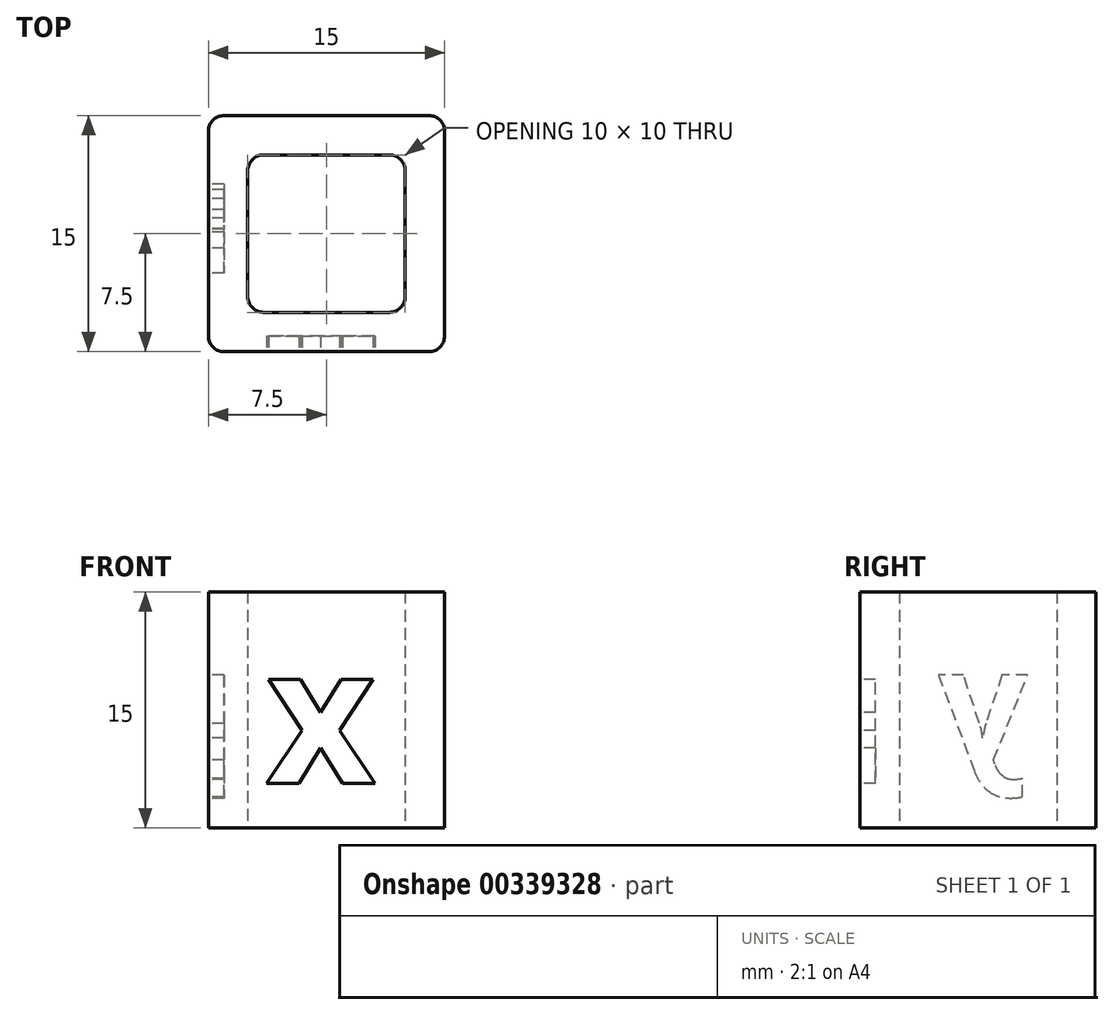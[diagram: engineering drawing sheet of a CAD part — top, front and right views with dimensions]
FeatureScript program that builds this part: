
annotation { "Feature Type Name" : "Feature", "Feature Type Description" : "" }
export const myFeature = defineFeature(function(context is Context, id is Id, definition is map)
    precondition{}
    {
        {
            var Q0;
            Q0=qCreatedBy(makeId("Top.planeOp"),FACE);
            var sketch = newSketch(context, id + "F0", { "sketchPlane" : qUnion([Q0])});
            skLineSegment(sketch, "E0.bottom", {"start": v(7.5, -7.5) * mm, "end": v(-7.5, -7.5) * mm});
            skLineSegment(sketch, "E0.top", {"start": v(7.5, 7.5) * mm, "end": v(-7.5, 7.5) * mm});
            skLineSegment(sketch, "E0.left", {"start": v(7.5, -7.5) * mm, "end": v(7.5, 7.5) * mm});
            skLineSegment(sketch, "E0.right", {"start": v(-7.5, -7.5) * mm, "end": v(-7.5, 7.5) * mm});
            skPoint(sketch, "E0.middle", {"position": v(0, 0) * mm});
            skLineSegment(sketch, "E1.bottom", {"start": v(5, -5) * mm, "end": v(-5, -5) * mm});
            skLineSegment(sketch, "E1.top", {"start": v(5, 5) * mm, "end": v(-5, 5) * mm});
            skLineSegment(sketch, "E1.left", {"start": v(5, -5) * mm, "end": v(5, 5) * mm});
            skLineSegment(sketch, "E1.right", {"start": v(-5, -5) * mm, "end": v(-5, 5) * mm});
            skSolve(sketch);
        }
        {
            var Q0;
            Q0=makeQuery(id+"F0.imprint","IMPRINT",FACE,{"disambiguationData":[TD([[makeQuery(id+"F0.imprint","IMPRINT",EDGE,{"derivedFrom":sQuery(id+"F0.wireOp",EDGE,"E0.bottom")}),-1.0]])]});
            extrude(context, id + "F1", {"entities" : qUnion([Q0]), "depth" : 15 * mm, "offsetDistance" : 25 * mm});
        }
        {
            var Q0;
            Q0=makeQuery(id+"F1.opExtrude","SWEPT_EDGE",EDGE,{"disambiguationData":[OSD([sQuery(id+"F0.wireOp",EDGE,"E0.top"),sQuery(id+"F0.wireOp",EDGE,"E0.right")])]});
            var Q1;
            Q1=makeQuery(id+"F1.opExtrude","SWEPT_EDGE",EDGE,{"disambiguationData":[OSD([sQuery(id+"F0.wireOp",EDGE,"E0.bottom"),sQuery(id+"F0.wireOp",EDGE,"E0.right")])]});
            var Q2;
            Q2=makeQuery(id+"F1.opExtrude","SWEPT_EDGE",EDGE,{"disambiguationData":[OSD([sQuery(id+"F0.wireOp",EDGE,"E0.bottom"),sQuery(id+"F0.wireOp",EDGE,"E0.left")])]});
            var Q3;
            Q3=makeQuery(id+"F1.opExtrude","SWEPT_EDGE",EDGE,{"disambiguationData":[OSD([sQuery(id+"F0.wireOp",EDGE,"E0.top"),sQuery(id+"F0.wireOp",EDGE,"E0.left")])]});
            var Q4;
            Q4=makeQuery(id+"F1.opExtrude","SWEPT_EDGE",EDGE,{"disambiguationData":[OSD([sQuery(id+"F0.wireOp",EDGE,"E1.top"),sQuery(id+"F0.wireOp",EDGE,"E1.left")])]});
            var Q5;
            Q5=makeQuery(id+"F1.opExtrude","SWEPT_EDGE",EDGE,{"disambiguationData":[OSD([sQuery(id+"F0.wireOp",EDGE,"E1.top"),sQuery(id+"F0.wireOp",EDGE,"E1.right")])]});
            var Q6;
            Q6=makeQuery(id+"F1.opExtrude","SWEPT_EDGE",EDGE,{"disambiguationData":[OSD([sQuery(id+"F0.wireOp",EDGE,"E1.bottom"),sQuery(id+"F0.wireOp",EDGE,"E1.left")])]});
            var Q7;
            Q7=makeQuery(id+"F1.opExtrude","SWEPT_EDGE",EDGE,{"disambiguationData":[OSD([sQuery(id+"F0.wireOp",EDGE,"E1.bottom"),sQuery(id+"F0.wireOp",EDGE,"E1.right")])]});
            fillet(context, id + "F2", {"entities" : qUnion([Q0, Q1, Q2, Q3, Q4, Q5, Q6, Q7]), "radius" : 1 * mm, "allowEdgeOverflow" : false});
        }
        {
            var Q0;
            Q0=makeQuery(id+"F1.opExtrude","SWEPT_FACE",FACE,{"disambiguationData":[OSD([sQuery(id+"F0.wireOp",EDGE,"E0.bottom")])]});
            var sketch = newSketch(context, id + "F3", { "sketchPlane" : qUnion([Q0])});
            skPoint(sketch, "E2", {"position": v(-6.5, 7.5) * mm});
            skText(sketch, "E3", { "text": "x", "fontName": "OpenSans-Bold.ttf"});
            const initialGuessF3  = {"E3": [-0.00385, 0.00284, 1, 0, 0.00869]};
            skSetInitialGuess(sketch, initialGuessF3);
            skSolve(sketch);
        }
        {
            var Q0;
            Q0=makeQuery(id+"F1.opExtrude","SWEPT_FACE",FACE,{"disambiguationData":[OSD([sQuery(id+"F0.wireOp",EDGE,"E0.right")])]});
            var sketch = newSketch(context, id + "F4", { "sketchPlane" : qUnion([Q0])});
            skText(sketch, "E4", { "text": "y\n", "fontName": "OpenSans-Bold.ttf"});
            const initialGuessF4  = {"E4": [-0.00315, 0.00428, 1, 0, 0.00716]};
            skSetInitialGuess(sketch, initialGuessF4);
            skSolve(sketch);
        }
        {
            var Q0;
            Q0=makeQuery(id+"F4.imprint","IMPRINT",FACE,{"disambiguationData":[TD([[makeQuery(id+"F4.imprint","IMPRINT",EDGE,{"derivedFrom":sQuery(id+"F4.wireOp",EDGE,"E4.sketch_text.stroke-0")}),-1.0]])]});
            extrude(context, id + "F5", {"entities" : qUnion([Q0]), "operationType" : NewBodyOperationType.REMOVE, "oppositeDirection" : true, "depth" : 1 * mm, "offsetDistance" : 25 * mm});
        }
        {
            var Q0;
            Q0=makeQuery(id+"F3.imprint","IMPRINT",FACE,{"disambiguationData":[TD([[makeQuery(id+"F3.imprint","IMPRINT",EDGE,{"derivedFrom":sQuery(id+"F3.wireOp",EDGE,"E3.sketch_text.stroke-0")}),-1.0]])]});
            extrude(context, id + "F6", {"entities" : qUnion([Q0]), "operationType" : NewBodyOperationType.REMOVE, "oppositeDirection" : true, "depth" : 1 * mm, "offsetDistance" : 25 * mm});
        }
    });
